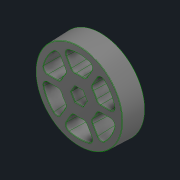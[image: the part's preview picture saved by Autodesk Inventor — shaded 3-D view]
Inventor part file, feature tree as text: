
AUTODESK INVENTOR PART (.ipt)
format: ipt  version: 2021 (Build 250183000, 183)  size: 740,864 bytes
history: native  units: in
note: dims shown in document units (in); Inventor stores cm internally (conversion verified against a paired STEP export)
features: fillet x1
ambient origin geometry x8: Origin, YZ Plane, XZ Plane, XY Plane, X Axis, Y Axis, Z Axis, Center Point
bodies: Solid1 (feature_tree)
feature tree (1):
  fillet  "Fillet3"  [1 undecoded]
note: 1 required parameter value undecoded (feature->parameter linkage not recoverable at this tier; creation-order binding heuristic only, values carry confidence <= 0.55)
